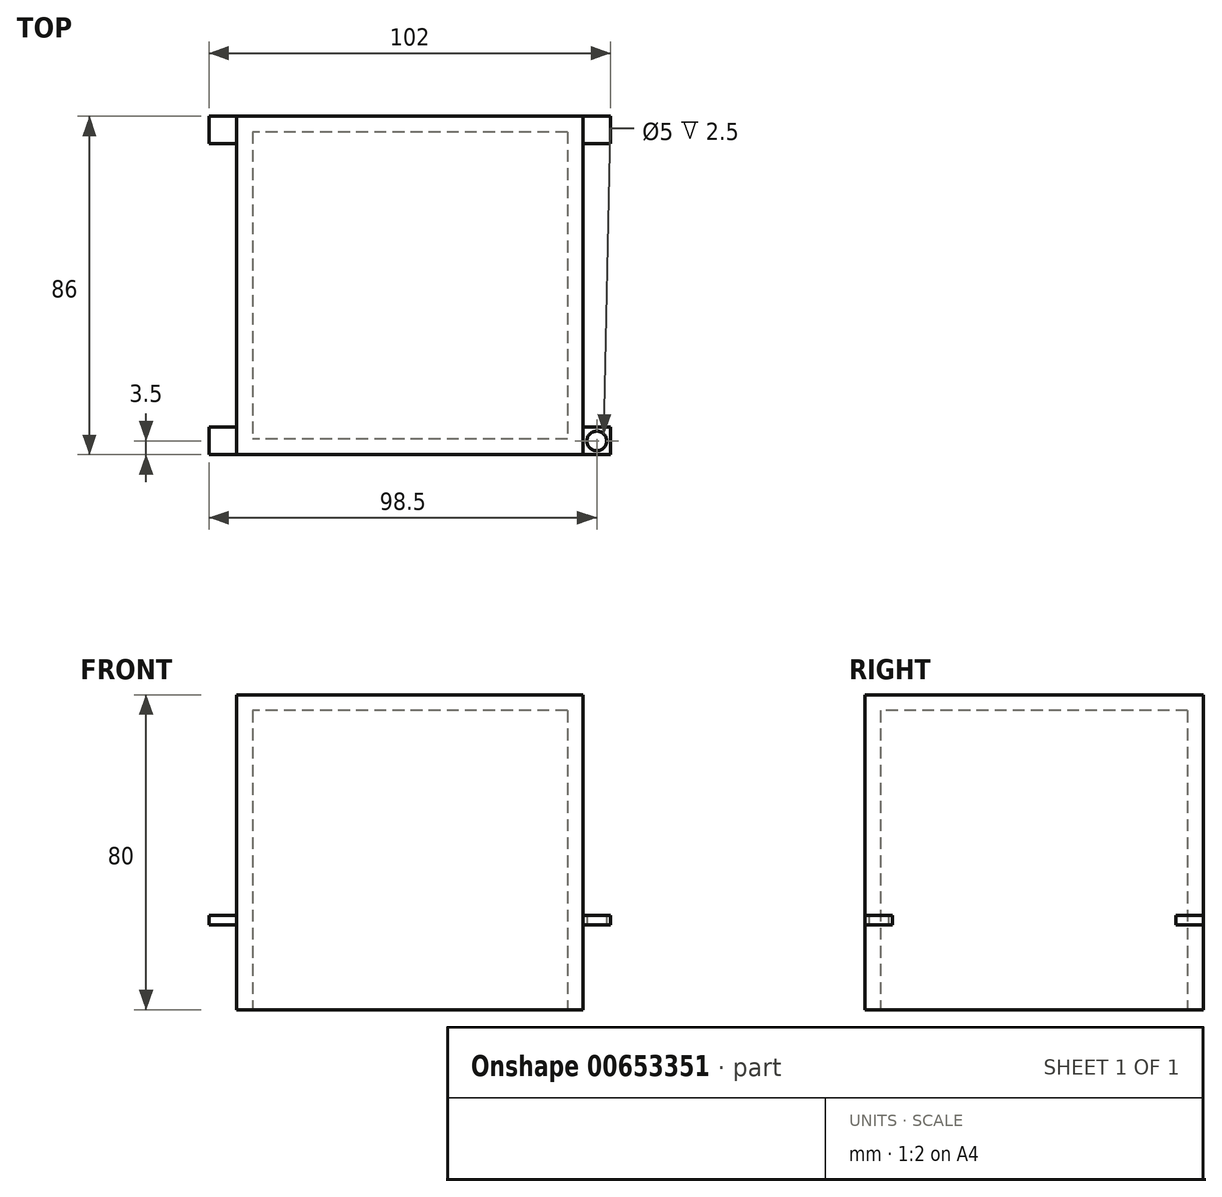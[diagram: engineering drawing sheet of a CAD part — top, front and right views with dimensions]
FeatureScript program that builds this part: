
annotation { "Feature Type Name" : "Feature", "Feature Type Description" : "" }
export const myFeature = defineFeature(function(context is Context, id is Id, definition is map)
    precondition{}
    {
        {
            var Q0;
            Q0=qCreatedBy(makeId("Top.planeOp"),FACE);
            var sketch = newSketch(context, id + "F0", { "sketchPlane" : qUnion([Q0])});
            skLineSegment(sketch, "E0.bottom", {"start": v(44, 43) * mm, "end": v(-44, 43) * mm});
            skLineSegment(sketch, "E0.top", {"start": v(44, -43) * mm, "end": v(-44, -43) * mm});
            skLineSegment(sketch, "E0.left", {"start": v(44, 43) * mm, "end": v(44, -43) * mm});
            skLineSegment(sketch, "E0.right", {"start": v(-44, 43) * mm, "end": v(-44, -43) * mm});
            skPoint(sketch, "E0.middle", {"position": v(0, 0) * mm});
            skPoint(sketch, "E1", {"position": v(0, -43) * mm});
            skPoint(sketch, "E2", {"position": v(37, 43) * mm});
            skPoint(sketch, "E3", {"position": v(37, -43) * mm});
            skPoint(sketch, "E4", {"position": v(-37, 43) * mm});
            skPoint(sketch, "E5", {"position": v(-37, -43) * mm});
            skLineSegment(sketch, "E6.bottom", {"start": v(-44, 43) * mm, "end": v(-37, 43) * mm});
            skLineSegment(sketch, "E7.bottom", {"start": v(44, 43) * mm, "end": v(37, 43) * mm});
            skLineSegment(sketch, "E8.bottom", {"start": v(-44, -43) * mm, "end": v(-37, -43) * mm});
            skLineSegment(sketch, "E9.bottom", {"start": v(44, -43) * mm, "end": v(37, -43) * mm});
            skSolve(sketch);
        }
        {
            var Q0;
            Q0=makeQuery(id+"F0.imprint","IMPRINT",FACE,{"disambiguationData":[TD([[makeQuery(id+"F0.imprint","IMPRINT",EDGE,{"derivedFrom":sQuery(id+"F0.wireOp",EDGE,"E0.bottom")}),1.0]])]});
            extrude(context, id + "F1", {"entities" : qUnion([Q0]), "depth" : 80 * mm, "offsetDistance" : 25 * mm});
        }
        {
            var Q0;
            Q0=qCreatedBy(makeId("Right.planeOp"),FACE);
            var sketch = newSketch(context, id + "F2", { "sketchPlane" : qUnion([Q0])});
            skPoint(sketch, "E10", {"position": v(-43, 0) * mm});
            skPoint(sketch, "E11", {"position": v(-43, 18.78) * mm});
            skSolve(sketch);
        }
        {
            var Q0;
            Q0=sQuery(id+"F2.wireOp",VERTEX,"E11");
            var Q1;
            Q1=sQuery(id+"F0.wireOp",VERTEX,"E1");
            var Q2;
            Q2=sQuery(id+"F0.wireOp",VERTEX,"E3");
            cPlane(context, id + "F3", {"entities" : qUnion([Q0, Q1, Q2]), "cplaneType" : CPlaneType.THREE_POINT, "offset" : 25 * mm, "width" : 150 * mm, "height" : 150 * mm});
        }
        {
            var Q0;
            Q0=qCreatedBy(id+"F3.planeOp",FACE);
            var sketch = newSketch(context, id + "F4", { "sketchPlane" : qUnion([Q0])});
            skPoint(sketch, "E12", {"position": v(0, 21.5) * mm});
            skSolve(sketch);
        }
        {
            var Q0;
            Q0=qCreatedBy(makeId("Front.planeOp"),FACE);
            var sketch = newSketch(context, id + "F5", { "sketchPlane" : qUnion([Q0])});
            skPoint(sketch, "E13", {"position": v(0, 21.5) * mm});
            skPoint(sketch, "E14", {"position": v(4.96, 0) * mm});
            skPoint(sketch, "E15", {"position": v(4.96, 21.5) * mm});
            skSolve(sketch);
        }
        {
            var Q0;
            Q0=sQuery(id+"F5.wireOp",VERTEX,"E13");
            var Q1;
            Q1=sQuery(id+"F5.wireOp",VERTEX,"E15");
            var Q2;
            Q2=sQuery(id+"F4.wireOp",VERTEX,"E12");
            cPlane(context, id + "F6", {"entities" : qUnion([Q0, Q1, Q2]), "cplaneType" : CPlaneType.THREE_POINT, "offset" : 25 * mm, "width" : 150 * mm, "height" : 150 * mm});
        }
        {
            var Q0;
            Q0=qCreatedBy(id+"F6.planeOp",FACE);
            var sketch = newSketch(context, id + "F7", { "sketchPlane" : qUnion([Q0])});
            skLineSegment(sketch, "E16.bottom", {"start": v(44, 43) * mm, "end": v(-44, 43) * mm});
            skLineSegment(sketch, "E16.top", {"start": v(44, -43) * mm, "end": v(-44, -43) * mm});
            skLineSegment(sketch, "E16.left", {"start": v(44, 43) * mm, "end": v(44, -43) * mm});
            skLineSegment(sketch, "E16.right", {"start": v(-44, 43) * mm, "end": v(-44, -43) * mm});
            skPoint(sketch, "E16.middle", {"position": v(0, 0) * mm});
            skPoint(sketch, "E17", {"position": v(-51, 43) * mm});
            skPoint(sketch, "E18", {"position": v(-51, 36) * mm});
            skLineSegment(sketch, "E19", {"start": v(-51, 36) * mm, "end": v(-44, 36) * mm});
            skLineSegment(sketch, "E20", {"start": v(-44, 36) * mm, "end": v(-51, 43) * mm});
            skLineSegment(sketch, "E21", {"start": v(-51, 36) * mm, "end": v(-51, 43) * mm});
            skLineSegment(sketch, "E22", {"start": v(-44, 43) * mm, "end": v(-51, 43) * mm});
            skLineSegment(sketch, "E23", {"start": v(-44, 43) * mm, "end": v(-51, 36) * mm});
            skPoint(sketch, "E24", {"position": v(-47.5, 39.5) * mm});
            skLineSegment(sketch, "E25.MirrorCS", {"start": v(44, 43) * mm, "end": v(51, 43) * mm});
            skLineSegment(sketch, "E26.MirrorCS", {"start": v(51, 36) * mm, "end": v(51, 43) * mm});
            skLineSegment(sketch, "E27.MirrorCS", {"start": v(44, 36) * mm, "end": v(51, 43) * mm});
            skLineSegment(sketch, "E28.MirrorCS", {"start": v(51, 36) * mm, "end": v(44, 36) * mm});
            skPoint(sketch, "E29.MirrorP", {"position": v(47.5, 39.5) * mm});
            skLineSegment(sketch, "E30.MirrorCS", {"start": v(44, 43) * mm, "end": v(51, 36) * mm});
            skLineSegment(sketch, "E31.MirrorCS", {"start": v(-44, -43) * mm, "end": v(-51, -43) * mm});
            skLineSegment(sketch, "E32.MirrorCS", {"start": v(-44, -36) * mm, "end": v(-51, -43) * mm});
            skLineSegment(sketch, "E33.MirrorCS", {"start": v(-44, -43) * mm, "end": v(-51, -36) * mm});
            skPoint(sketch, "E34.MirrorP", {"position": v(-47.5, -39.5) * mm});
            skLineSegment(sketch, "E35.MirrorCS", {"start": v(-51, -36) * mm, "end": v(-44, -36) * mm});
            skLineSegment(sketch, "E36.MirrorCS", {"start": v(-51, -36) * mm, "end": v(-51, -43) * mm});
            skLineSegment(sketch, "E37.MirrorCS", {"start": v(51, -36) * mm, "end": v(44, -36) * mm});
            skLineSegment(sketch, "E38.MirrorCS", {"start": v(44, -43) * mm, "end": v(51, -43) * mm});
            skLineSegment(sketch, "E39.MirrorCS", {"start": v(51, -36) * mm, "end": v(51, -43) * mm});
            skLineSegment(sketch, "E40.MirrorCS", {"start": v(44, -43) * mm, "end": v(51, -36) * mm});
            skLineSegment(sketch, "E41.MirrorCS", {"start": v(44, -36) * mm, "end": v(51, -43) * mm});
            skPoint(sketch, "E42.MirrorP", {"position": v(47.5, -39.5) * mm});
            skSolve(sketch);
        }
        {
            var Q0;
            {var subQ0=sQuery(id+"F7.wireOp",EDGE,"E21");Q0=makeQuery(id+"F7.imprint","IMPRINT",FACE,{"disambiguationData":[TD([[makeQuery(id+"F7.imprint","IMPRINT",EDGE,{"derivedFrom":subQ0}),-1.0]])]});}
            var Q1;
            {var subQ0=sQuery(id+"F7.wireOp",EDGE,"E19");Q1=makeQuery(id+"F7.imprint","IMPRINT",FACE,{"disambiguationData":[TD([[makeQuery(id+"F7.imprint","IMPRINT",EDGE,{"derivedFrom":subQ0}),1.0]])]});}
            var Q2;
            {var subQ0=sQuery(id+"F7.wireOp",EDGE,"E23");var subQ3=sQuery(id+"F7.wireOp",EDGE,"E20");var subQ5=makeQuery(id+"F7.imprint","INTERSECT",VERTEX,{"derivedFrom":[subQ3,subQ0]});Q2=makeQuery(id+"F7.imprint","IMPRINT",FACE,{"disambiguationData":[TD([[makeQuery(id+"F7.imprint","IMPRINT",EDGE,{"disambiguationData":[TD([[subQ5,1.0]])],"derivedFrom":subQ3}),-1.0]])]});}
            var Q3;
            {var subQ0=sQuery(id+"F7.wireOp",EDGE,"E22");Q3=makeQuery(id+"F7.imprint","IMPRINT",FACE,{"disambiguationData":[TD([[makeQuery(id+"F7.imprint","IMPRINT",EDGE,{"derivedFrom":subQ0}),1.0]])]});}
            var Q4;
            {var subQ0=sQuery(id+"F7.wireOp",EDGE,"E25.MirrorCS");Q4=makeQuery(id+"F7.imprint","IMPRINT",FACE,{"disambiguationData":[TD([[makeQuery(id+"F7.imprint","IMPRINT",EDGE,{"derivedFrom":subQ0}),-1.0]])]});}
            var Q5;
            {var subQ0=sQuery(id+"F7.wireOp",EDGE,"E28.MirrorCS");Q5=makeQuery(id+"F7.imprint","IMPRINT",FACE,{"disambiguationData":[TD([[makeQuery(id+"F7.imprint","IMPRINT",EDGE,{"derivedFrom":subQ0}),-1.0]])]});}
            var Q6;
            {var subQ0=sQuery(id+"F7.wireOp",EDGE,"E26.MirrorCS");Q6=makeQuery(id+"F7.imprint","IMPRINT",FACE,{"disambiguationData":[TD([[makeQuery(id+"F7.imprint","IMPRINT",EDGE,{"derivedFrom":subQ0}),1.0]])]});}
            var Q7;
            {var subQ0=sQuery(id+"F7.wireOp",EDGE,"E30.MirrorCS");var subQ3=sQuery(id+"F7.wireOp",EDGE,"E27.MirrorCS");var subQ5=makeQuery(id+"F7.imprint","INTERSECT",VERTEX,{"derivedFrom":[subQ3,subQ0]});Q7=makeQuery(id+"F7.imprint","IMPRINT",FACE,{"disambiguationData":[TD([[makeQuery(id+"F7.imprint","IMPRINT",EDGE,{"disambiguationData":[TD([[subQ5,1.0]])],"derivedFrom":subQ3}),1.0]])]});}
            var Q8;
            {var subQ0=sQuery(id+"F7.wireOp",EDGE,"E38.MirrorCS");Q8=makeQuery(id+"F7.imprint","IMPRINT",FACE,{"disambiguationData":[TD([[makeQuery(id+"F7.imprint","IMPRINT",EDGE,{"derivedFrom":subQ0}),1.0]])]});}
            var Q9;
            {var subQ0=sQuery(id+"F7.wireOp",EDGE,"E37.MirrorCS");Q9=makeQuery(id+"F7.imprint","IMPRINT",FACE,{"disambiguationData":[TD([[makeQuery(id+"F7.imprint","IMPRINT",EDGE,{"derivedFrom":subQ0}),1.0]])]});}
            var Q10;
            {var subQ0=sQuery(id+"F7.wireOp",EDGE,"E39.MirrorCS");Q10=makeQuery(id+"F7.imprint","IMPRINT",FACE,{"disambiguationData":[TD([[makeQuery(id+"F7.imprint","IMPRINT",EDGE,{"derivedFrom":subQ0}),-1.0]])]});}
            var Q11;
            {var subQ0=sQuery(id+"F7.wireOp",EDGE,"E40.MirrorCS");var subQ3=sQuery(id+"F7.wireOp",EDGE,"E41.MirrorCS");var subQ5=makeQuery(id+"F7.imprint","INTERSECT",VERTEX,{"derivedFrom":[subQ0,subQ3]});Q11=makeQuery(id+"F7.imprint","IMPRINT",FACE,{"disambiguationData":[TD([[makeQuery(id+"F7.imprint","IMPRINT",EDGE,{"disambiguationData":[TD([[subQ5,1.0]])],"derivedFrom":subQ3}),-1.0]])]});}
            var Q12;
            {var subQ0=sQuery(id+"F7.wireOp",EDGE,"E33.MirrorCS");var subQ3=sQuery(id+"F7.wireOp",EDGE,"E32.MirrorCS");var subQ5=makeQuery(id+"F7.imprint","INTERSECT",VERTEX,{"derivedFrom":[subQ3,subQ0]});Q12=makeQuery(id+"F7.imprint","IMPRINT",FACE,{"disambiguationData":[TD([[makeQuery(id+"F7.imprint","IMPRINT",EDGE,{"disambiguationData":[TD([[subQ5,1.0]])],"derivedFrom":subQ3}),1.0]])]});}
            var Q13;
            {var subQ0=sQuery(id+"F7.wireOp",EDGE,"E35.MirrorCS");Q13=makeQuery(id+"F7.imprint","IMPRINT",FACE,{"disambiguationData":[TD([[makeQuery(id+"F7.imprint","IMPRINT",EDGE,{"derivedFrom":subQ0}),-1.0]])]});}
            var Q14;
            {var subQ0=sQuery(id+"F7.wireOp",EDGE,"E36.MirrorCS");Q14=makeQuery(id+"F7.imprint","IMPRINT",FACE,{"disambiguationData":[TD([[makeQuery(id+"F7.imprint","IMPRINT",EDGE,{"derivedFrom":subQ0}),1.0]])]});}
            var Q15;
            {var subQ0=sQuery(id+"F7.wireOp",EDGE,"E31.MirrorCS");Q15=makeQuery(id+"F7.imprint","IMPRINT",FACE,{"disambiguationData":[TD([[makeQuery(id+"F7.imprint","IMPRINT",EDGE,{"derivedFrom":subQ0}),-1.0]])]});}
            extrude(context, id + "F8", {"entities" : qUnion([Q0, Q1, Q2, Q3, Q4, Q5, Q6, Q7, Q8, Q9, Q10, Q11, Q12, Q13, Q14, Q15]), "depth" : 2.5 * mm, "offsetDistance" : 25 * mm});
        }
        {
            var Q0;
            Q0=makeQuery(id+"F1.opExtrude","CAP_FACE",FACE,{"disambiguationData":[OSD([sQuery(id+"F0.wireOp",EDGE,"E0.bottom"),sQuery(id+"F0.wireOp",EDGE,"E0.top"),sQuery(id+"F0.wireOp",EDGE,"E0.left"),sQuery(id+"F0.wireOp",EDGE,"E0.right"),sQuery(id+"F0.wireOp",EDGE,"E6.bottom"),sQuery(id+"F0.wireOp",EDGE,"E7.bottom"),sQuery(id+"F0.wireOp",EDGE,"E8.bottom"),sQuery(id+"F0.wireOp",EDGE,"E9.bottom")])],"isStart":true});
            shell(context, id + "F9", {"entities" : qUnion([Q0]), "thickness" : 4 * mm});
        }
        {
            var Q0;
            Q0=sQuery(id+"F7.wireOp",VERTEX,"E42.MirrorP");
            var Q1;
            Q1=sQuery(id+"F7.wireOp",VERTEX,"E29.MirrorP");
            var Q2;
            Q2=sQuery(id+"F7.wireOp",VERTEX,"E24");
            var Q3;
            Q3=sQuery(id+"F7.wireOp",VERTEX,"E34.MirrorP");
            var Q4;
            Q4=makeQuery(id+"F8.opExtrude","SWEPT_BODY",BODY,{"disambiguationData":[OSD([sQuery(id+"F7.wireOp",EDGE,"E16.left"),sQuery(id+"F7.wireOp",EDGE,"E37.MirrorCS"),sQuery(id+"F7.wireOp",EDGE,"E38.MirrorCS"),sQuery(id+"F7.wireOp",EDGE,"E39.MirrorCS")])]});
            hole(context, id + "F10", {"style" : HoleStyle.SIMPLE, "endStyle" : HoleEndStyle.THROUGH, "oppositeDirection" : true, "holeDiameter" : 5 * mm, "majorDiameter" : 5 * mm, "isTappedThrough" : true, "tappedDepth" : 12 * mm, "tapClearance" : 3, "locations" : qUnion([Q0, Q1, Q2, Q3]), "scope" : qUnion([Q4])});
        }
        {
            var Q0;
            Q0=qCreatedBy(makeId("Right.planeOp"),FACE);
            var sketch = newSketch(context, id + "F11", { "sketchPlane" : qUnion([Q0])});
            skPoint(sketch, "E43", {"position": v(0, 38.21) * mm});
            skSolve(sketch);
        }
        {
            var Q0;
            Q0=sQuery(id+"F0.wireOp",VERTEX,"E0.left.end");
            var Q1;
            Q1=sQuery(id+"F0.wireOp",VERTEX,"E7.bottom.start");
            var Q2;
            Q2=sQuery(id+"F7.wireOp",VERTEX,"E16.left.end");
            cPlane(context, id + "F12", {"entities" : qUnion([Q0, Q1, Q2]), "cplaneType" : CPlaneType.THREE_POINT, "offset" : 25 * mm, "width" : 150 * mm, "height" : 150 * mm});
        }
        {
            var Q0;
            Q0=qCreatedBy(id+"F12.planeOp",FACE);
            var sketch = newSketch(context, id + "F13", { "sketchPlane" : qUnion([Q0])});
            skPoint(sketch, "E44", {"position": v(0, 38.18) * mm});
            skSolve(sketch);
        }
        {
            var Q0;
            Q0=sQuery(id+"F13.wireOp",VERTEX,"E44");
            var Q1;
            Q1=makeQuery(id+"F8.opExtrude","SWEPT_BODY",BODY,{"disambiguationData":[OSD([sQuery(id+"F7.wireOp",EDGE,"E16.left"),sQuery(id+"F7.wireOp",EDGE,"E37.MirrorCS"),sQuery(id+"F7.wireOp",EDGE,"E38.MirrorCS"),sQuery(id+"F7.wireOp",EDGE,"E39.MirrorCS")])]});
            hole(context, id + "F14", {"style" : HoleStyle.SIMPLE, "endStyle" : HoleEndStyle.THROUGH, "oppositeDirection" : true, "holeDiameter" : 5 * mm, "majorDiameter" : 5 * mm, "isTappedThrough" : true, "tappedDepth" : 12 * mm, "tapClearance" : 3, "locations" : qUnion([Q0]), "scope" : qUnion([Q1])});
        }
        {
            var Q0;
            Q0=sQuery(id+"F11.wireOp",VERTEX,"E43");
            var Q1;
            Q1=makeQuery(id+"F8.opExtrude","SWEPT_BODY",BODY,{"disambiguationData":[OSD([sQuery(id+"F7.wireOp",EDGE,"E16.left"),sQuery(id+"F7.wireOp",EDGE,"E37.MirrorCS"),sQuery(id+"F7.wireOp",EDGE,"E38.MirrorCS"),sQuery(id+"F7.wireOp",EDGE,"E39.MirrorCS")])]});
            hole(context, id + "F15", {"style" : HoleStyle.SIMPLE, "endStyle" : HoleEndStyle.THROUGH, "holeDiameter" : 5 * mm, "majorDiameter" : 5 * mm, "isTappedThrough" : true, "tappedDepth" : 12 * mm, "tapClearance" : 3, "locations" : qUnion([Q0]), "scope" : qUnion([Q1])});
        }
    });
